# Revit family: Screens-Teknion-JNSELE_Felt_End_Screen-R2018
name_source: partatom
category: Furniture
revit_build: Autodesk Revit 2018 (Build: 20190510_1515(x64)
units: mm (PartAtom-declared; Revit-internal decimal feet)

## family parameters
Always vertical = Yes
Cut with Voids When Loaded = No
OmniClass Number = 23.40.20.00
OmniClass Title = General Furniture and Specialties
Room Calculation Point = No
Shared = Yes
Work Plane-Based = No

## types (3) — shared parameters
Assembly Code = E2020200
Manufacturer = Teknion
Manufacturer Fax = 416.661.4586
Part Number = JNSELE
Product Documentation Link = https://www.teknion.com
Product Line = Expansion Cityline
Product Page URL = https://www.teknion.com
Series = Expansion Cityline
Sustainability Data = https://www.teknion.com
URL = www.teknion.com
Unit Weight URL = http://www.teknion.com
Warranty = http://www.teknion.com

## per-type parameters (varying)
| type | Angled Leg on the Left | Angled Leg on the Right | Description | Height Adjustable Table | Model |
| Height-Adjustable Table Mounting Style | No | No | Felt End Screen, Height-Adjustable Table Mounting Style, 18" Modesty Base Height from Floor, 42" Datum Height, Radius Corner Detail | Yes | JNSELEH1842__R |
| Angled Leg on Left Side Mounting Style | Yes | No | Felt End Screen, Angled Leg on Left Side Mounting Style, 18" Modesty Base Height from Floor, 42" Datum Height, Radius Corner Detail | No | JNSELEL1842__R |
| Angled Leg on Right Side Mounting Style | No | Yes | Felt End Screen, Angled Leg on Right Side Mounting Style, 18" Modesty Base Height from Floor, 42" Datum Height, Radius Corner Detail | No | JNSELER1842__R |

## geometry (parser evidence)
native form markers: Sweep x2
no freeform markers — native parametric forms only
